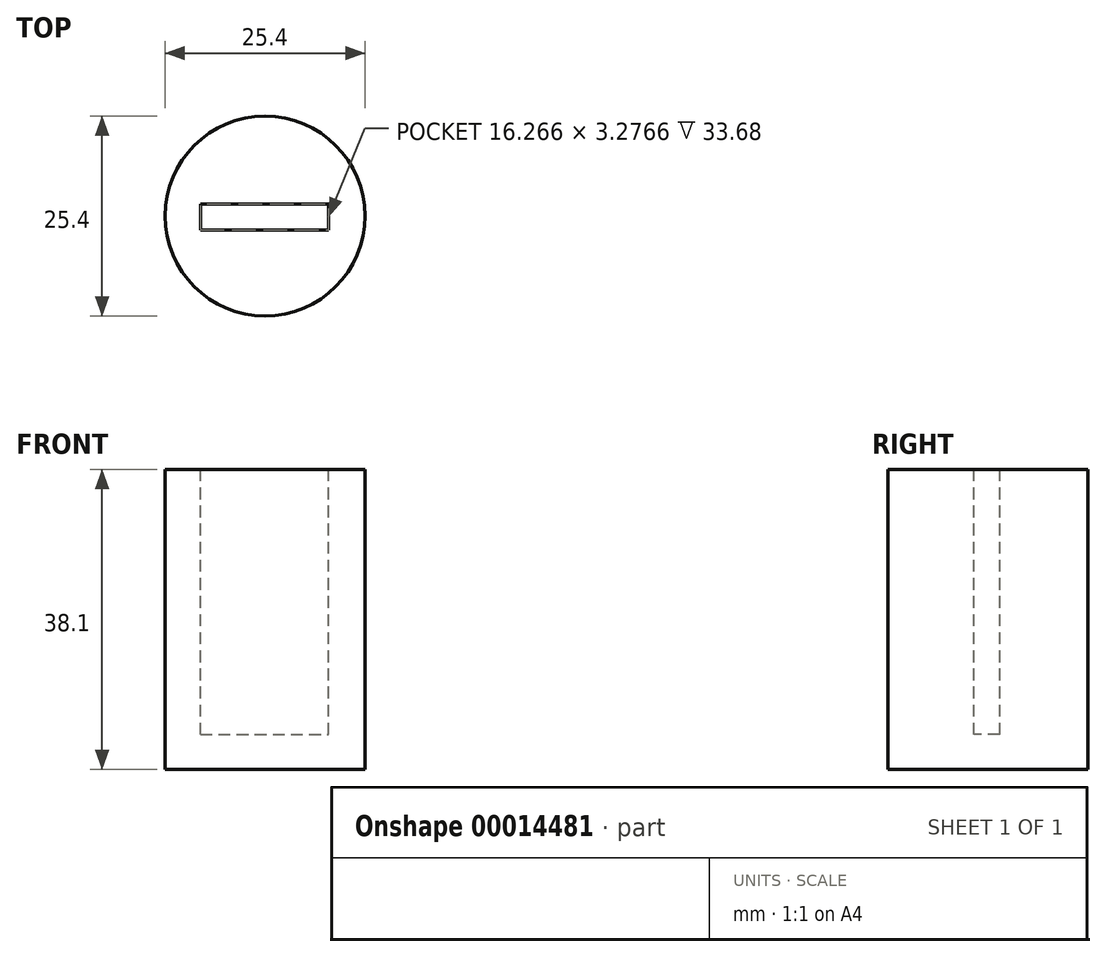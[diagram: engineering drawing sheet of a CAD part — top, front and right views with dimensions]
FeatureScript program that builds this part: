
annotation { "Feature Type Name" : "Feature", "Feature Type Description" : "" }
export const myFeature = defineFeature(function(context is Context, id is Id, definition is map)
    precondition{}
    {
        {
            var Q0;
            Q0=qCreatedBy(makeId("Top.planeOp"),FACE);
            var sketch = newSketch(context, id + "F0", { "sketchPlane" : qUnion([Q0])});
            skCircle(sketch, "E0", {"center": v(0, 0) * mm, "radius": 12.7 * mm});
            skSolve(sketch);
        }
        {
            var Q0;
            Q0=makeQuery(id+"F0.imprint","IMPRINT",FACE,{"disambiguationData":[TD([[makeQuery(id+"F0.imprint","IMPRINT",EDGE,{"derivedFrom":sQuery(id+"F0.wireOp",EDGE,"E0")}),1.0]])]});
            extrude(context, id + "F1", {"entities" : qUnion([Q0]), "depth" : 25.4 * mm});
        }
        {
            var Q0;
            Q0=makeQuery(id+"F1.opExtrude","CAP_FACE",FACE,{"disambiguationData":[OSD([sQuery(id+"F0.wireOp",EDGE,"E0")])],"isStart":false});
            var sketch = newSketch(context, id + "F2", { "sketchPlane" : qUnion([Q0])});
            skLineSegment(sketch, "E1.bottom", {"start": v(-8.2, 1.5) * mm, "end": v(8.06, 1.5) * mm});
            skLineSegment(sketch, "E1.top", {"start": v(-8.2, -1.78) * mm, "end": v(8.06, -1.78) * mm});
            skLineSegment(sketch, "E1.left", {"start": v(-8.2, 1.5) * mm, "end": v(-8.2, -1.78) * mm});
            skLineSegment(sketch, "E1.right", {"start": v(8.06, 1.5) * mm, "end": v(8.06, -1.78) * mm});
            skSolve(sketch);
        }
        {
            var Q0;
            Q0=makeQuery(id+"F2.imprint","IMPRINT",FACE,{"disambiguationData":[TD([[makeQuery(id+"F2.imprint","IMPRINT",EDGE,{"derivedFrom":sQuery(id+"F2.wireOp",EDGE,"E1.bottom")}),-1.0]])]});
            extrude(context, id + "F3", {"entities" : qUnion([Q0]), "operationType" : NewBodyOperationType.REMOVE, "oppositeDirection" : true, "depth" : 20.98 * mm});
        }
        {
            var Q0;
            Q0=makeQuery(id+"F1.opExtrude","CAP_FACE",FACE,{"disambiguationData":[OSD([sQuery(id+"F0.wireOp",EDGE,"E0")])],"isStart":false});
            extrude(context, id + "F4", {"entities" : qUnion([Q0]), "operationType" : NewBodyOperationType.ADD, "depth" : 12.7 * mm});
        }
    });
